# Revit family: KEUCO_53902010000_
name_source: partatom
category: Plumbing Fixtures
revit_build: Autodesk Revit 2016 (Build: 20150220_1215(x64)
units: mm (PartAtom-declared; Revit-internal decimal feet)

## family parameters
Always vertical = Yes
Cut with Voids When Loaded = No
OmniClass Number = 23.45.00.00
OmniClass Title = Sanitary, Laundry, and Cleaning Equipment
Part Type = Normal
Room Calculation Point = No
Round Connector Dimension = Use Diameter
Shared = No
Work Plane-Based = Yes

## types (2) — shared parameters
Ausschreibungstext = KEUCO PLAN BLUE Einhebel-Waschtischmischer 90, 53902010000
hochglanzverchromter Einhebel-Waschtischmischer, 
in ästhetischem, funktionalem Design, 
für Standmontage, inklusive Zugstangen-Ablaufgarnitur,
hochwertige Mischwasserkartusche mit 
keramischen Dichtscheiben und Temperaturbegrenzung,
Durchflussmenge begrenzt auf 6 l/min.,
Betätigungselement aus Metall,
Einlochmontage mit Schnell-Montage-System 
für Waschtische, bzw. Waschtischplatten mit 
einer maximalen Stärke von 40 mm,
Luftsprudler M 24x1, Strahlwinkel verstellbar +/- 8°,
Höhe 161 mm, Auslaufhöhe 84 mm, Ausladung 144 mm,
Grundkörperdurchmesser 48 mm, Auslaufdurchmesser 28 mm
Wasseranschluss mit flexiblen Druckschläuchen, 
Länge 420 mm, Gewindedurchmesser G 3/8 Zoll,
Anschlussrohrlänge 350 mm,
Zugstangen-Ablaufgarnitur mit 
G 1 1/4 Zoll Anschlussgewinde,
Länge der Zugstange 400 mm,
Abdeckstopfen Durchmesser 63 mm
DVGW geprüft
Default Elevation = 1219 mm
Description = mit Zugstangen-Ablaufgarnitur 1 1/4 Zoll
Einlochmontage mit Schnell-Montage-System
Mischwasserkartusche mit keramischen Dichtscheiben
und Temperaturbegrenzung
Luftsprudler M 24x1, Strahlwinkel verstellbar +/- 8°
Druckschläuche 570 mm G 3/8 Zoll
Durchflussmenge begrenzt auf 6 l/min.
geräuschgeprüft
Gewicht = 858
Kategorie = ARM
Manufacturer = KEUCO
Preisgruppe = 1
URL = https://www.keuco.com
Verwendung = GWC / WP

## per-type parameters (varying)
| type | Material Wasserhahn |
| 53902010000 | 23589001 Chrome |
| 53902170000 | Aluminium 1100-H18 |

note: column(s) folded — value = type name in every type: Artikelnummer

## geometry (parser evidence)
native form markers: Sweep x1
no freeform markers — native parametric forms only
